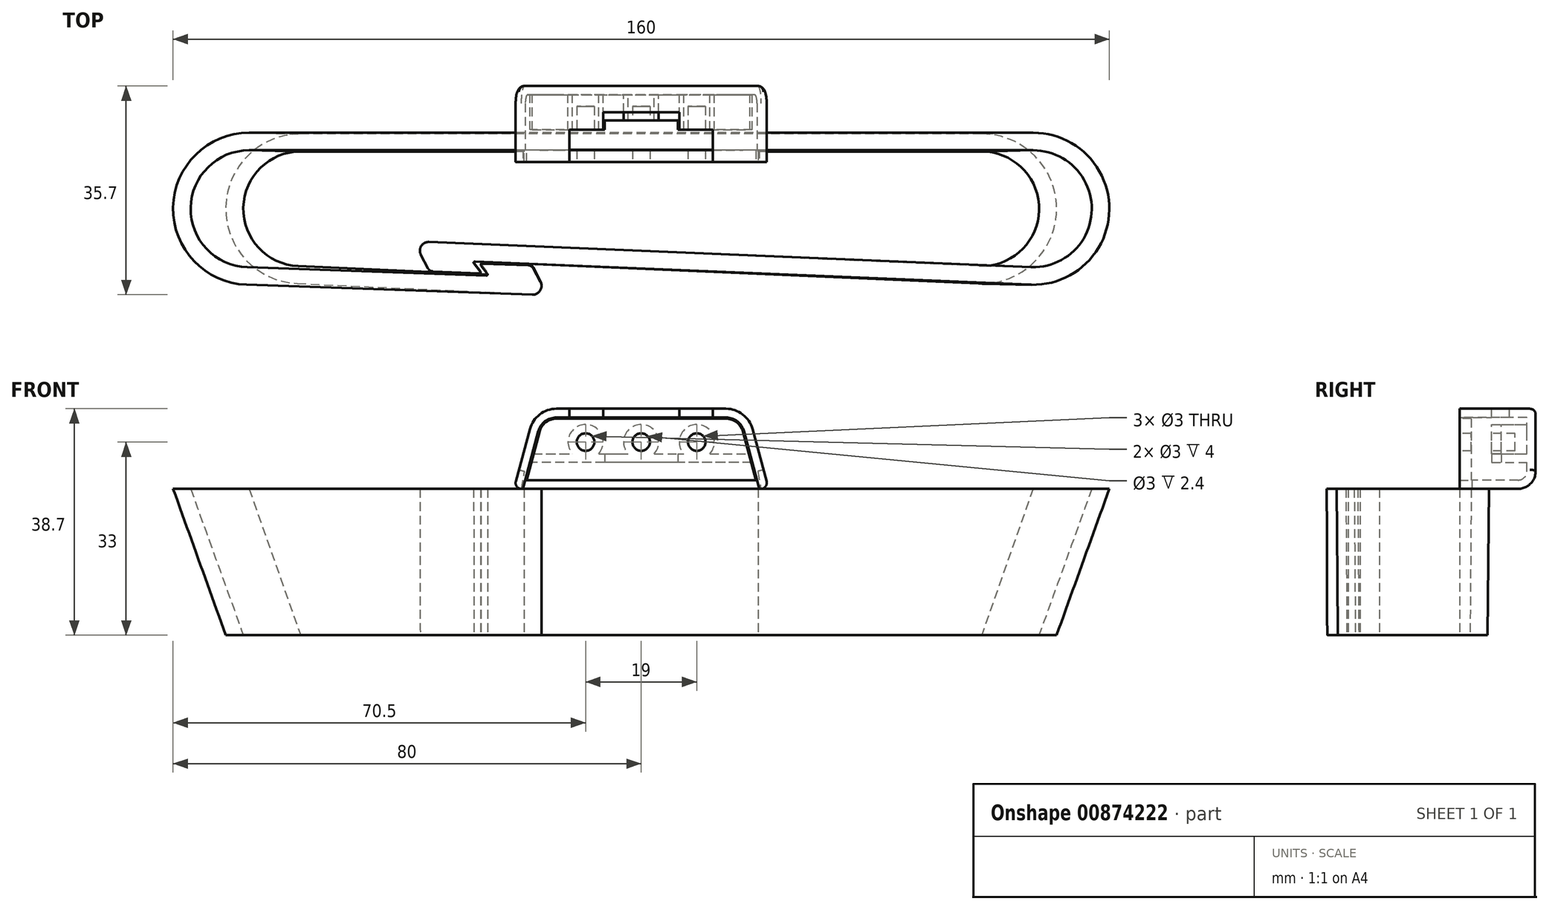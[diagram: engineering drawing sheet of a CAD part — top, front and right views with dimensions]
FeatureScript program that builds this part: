
annotation { "Feature Type Name" : "Feature", "Feature Type Description" : "" }
export const myFeature = defineFeature(function(context is Context, id is Id, definition is map)
    precondition{}
    {
        {
            var Q0;
            Q0=qCreatedBy(makeId("Top.planeOp"),FACE);
            var sketch = newSketch(context, id + "F0", { "sketchPlane" : qUnion([Q0])});
            skPoint(sketch, "E0.middle", {"position": v(0, 0) * mm});
            skArc(sketch, "E1", {"start": v(66.46, -12.99) * mm, "mid": v(80, -0.27) * mm, "end": v(67, 13) * mm});
            skLineSegment(sketch, "E2", {"start": v(67, 13) * mm, "end": v(-67, 13) * mm});
            skArc(sketch, "E3", {"start": v(-67, 13) * mm, "mid": v(-80, 0.23) * mm, "end": v(-67.45, -13) * mm});
            skLineSegment(sketch, "E4", {"start": v(66.46, -12.99) * mm, "end": v(-28.42, -9.01) * mm});
            skLineSegment(sketch, "E5", {"start": v(0, 13) * mm, "end": v(0, -10.2) * mm, "construction": true});
            skLineSegment(sketch, "E6", {"start": v(-16, 0) * mm, "end": v(-16, -14.79) * mm, "construction": true});
            skLineSegment(sketch, "E7", {"start": v(-67.45, -13) * mm, "end": v(-18.6, -14.7) * mm});
            skLineSegment(sketch, "E8", {"start": v(-67, 0) * mm, "end": v(-16, 0) * mm, "construction": true});
            skLineSegment(sketch, "E9.0", {"start": v(66.58, -10) * mm, "end": v(-36.26, -5.68) * mm});
            skLineSegment(sketch, "E9.1", {"start": v(-67.35, -10) * mm, "end": v(-26.46, -11.42) * mm});
            skArc(sketch, "E9.2", {"start": v(-67, 10) * mm, "mid": v(-77, 0.17) * mm, "end": v(-67.35, -10) * mm});
            skLineSegment(sketch, "E9.3", {"start": v(67, 10) * mm, "end": v(-67, 10) * mm});
            skArc(sketch, "E9.4", {"start": v(66.58, -10) * mm, "mid": v(77, -0.2) * mm, "end": v(67, 10) * mm});
            skLineSegment(sketch, "E10", {"start": v(-27.2, -9.4) * mm, "end": v(-19.29, -9.67) * mm});
            skLineSegment(sketch, "E11", {"start": v(-18.44, -10.2) * mm, "end": v(-17.22, -12.5) * mm});
            skPoint(sketch, "E12.visualSharp", {"position": v(-16, -14.79) * mm});
            skArc(sketch, "E12.filletArc", {"start": v(-18.6, -14.7) * mm, "mid": v(-17.27, -14) * mm, "end": v(-17.22, -12.5) * mm});
            skPoint(sketch, "E13.visualSharp", {"position": v(-18.71, -9.7) * mm});
            skArc(sketch, "E13.filletArc", {"start": v(-18.44, -10.2) * mm, "mid": v(-18.8, -9.82) * mm, "end": v(-19.29, -9.67) * mm});
            skPoint(sketch, "E14.visualSharp", {"position": v(-27.2, -9.4) * mm});
            skArc(sketch, "E14.filletArc", {"start": v(-27.2, -9.4) * mm, "mid": v(-27.4, -9.5) * mm, "end": v(-27.37, -9.72) * mm});
            skLineSegment(sketch, "E15", {"start": v(0, 0) * mm, "end": v(67, 0) * mm, "construction": true});
            skLineSegment(sketch, "E16", {"start": v(-28.59, -9.33) * mm, "end": v(-27.52, -10.72) * mm});
            skLineSegment(sketch, "E17", {"start": v(-27.69, -11.04) * mm, "end": v(-35.6, -10.71) * mm});
            skLineSegment(sketch, "E18", {"start": v(-36.45, -10.18) * mm, "end": v(-37.65, -7.87) * mm});
            skPoint(sketch, "E19.visualSharp", {"position": v(-36.18, -10.69) * mm});
            skArc(sketch, "E19.filletArc", {"start": v(-36.45, -10.18) * mm, "mid": v(-36.1, -10.56) * mm, "end": v(-35.6, -10.71) * mm});
            skPoint(sketch, "E20.visualSharp", {"position": v(-38.85, -5.57) * mm});
            skArc(sketch, "E20.filletArc", {"start": v(-36.26, -5.68) * mm, "mid": v(-37.59, -6.38) * mm, "end": v(-37.65, -7.87) * mm});
            skArc(sketch, "E21.filletArc", {"start": v(-27.69, -11.04) * mm, "mid": v(-27.5, -10.94) * mm, "end": v(-27.52, -10.72) * mm});
            skPoint(sketch, "E22.visualSharp", {"position": v(-28.85, -9) * mm});
            skArc(sketch, "E22.filletArc", {"start": v(-28.42, -9.01) * mm, "mid": v(-28.6, -9.12) * mm, "end": v(-28.59, -9.33) * mm});
            skLineSegment(sketch, "E23", {"start": v(-16, 0) * mm, "end": v(0, 0) * mm, "construction": true});
            skArc(sketch, "E24", {"start": v(-26.46, -11.42) * mm, "mid": v(-26.27, -11.31) * mm, "end": v(-26.3, -11.1) * mm});
            skLineSegment(sketch, "E25", {"start": v(-27.37, -9.72) * mm, "end": v(-26.3, -11.1) * mm});
            skLineSegment(sketch, "E26", {"start": v(-27.37, -9.47) * mm, "end": v(-27.37, -10.97) * mm, "construction": true});
            skLineSegment(sketch, "E27", {"start": v(-27.52, -10.72) * mm, "end": v(-27.52, -9.22) * mm, "construction": true});
            skSolve(sketch);
        }
        {
            var Q0;
            Q0=qCreatedBy(makeId("Top.planeOp"),FACE);
            cPlane(context, id + "F1", {"entities" : qUnion([Q0]), "cplaneType" : CPlaneType.OFFSET, "offset" : 25 * mm, "oppositeDirection" : true, "width" : 150 * mm, "height" : 150 * mm});
        }
        {
            var Q0;
            Q0=qCreatedBy(id+"F1.planeOp",FACE);
            var sketch = newSketch(context, id + "F2", { "sketchPlane" : qUnion([Q0])});
            skPoint(sketch, "E28.middle", {"position": v(0, 0) * mm});
            skArc(sketch, "E29", {"start": v(57.64, -12.79) * mm, "mid": v(71, -0.28) * mm, "end": v(58.2, 12.8) * mm});
            skLineSegment(sketch, "E30", {"start": v(58.2, 12.8) * mm, "end": v(-58.2, 12.8) * mm});
            skArc(sketch, "E31", {"start": v(-58.2, 12.8) * mm, "mid": v(-71, 0.3) * mm, "end": v(-58.78, -12.79) * mm});
            skLineSegment(sketch, "E32", {"start": v(57.64, -12.79) * mm, "end": v(-28.37, -9.03) * mm});
            skLineSegment(sketch, "E33", {"start": v(0, 12.8) * mm, "end": v(0, -10.27) * mm, "construction": true});
            skLineSegment(sketch, "E34", {"start": v(-16, 0) * mm, "end": v(-16, -14.73) * mm, "construction": true});
            skLineSegment(sketch, "E35", {"start": v(-58.78, -12.79) * mm, "end": v(-18.6, -14.61) * mm});
            skLineSegment(sketch, "E36", {"start": v(-58.2, 0) * mm, "end": v(-16, 0) * mm, "construction": true});
            skLineSegment(sketch, "E37.0", {"start": v(57.77, -9.8) * mm, "end": v(-36.2, -5.69) * mm});
            skLineSegment(sketch, "E37.1", {"start": v(-58.64, -9.79) * mm, "end": v(-26.42, -11.25) * mm});
            skArc(sketch, "E37.2", {"start": v(-58.2, 9.8) * mm, "mid": v(-68, 0.22) * mm, "end": v(-58.64, -9.79) * mm});
            skLineSegment(sketch, "E37.3", {"start": v(58.2, 9.8) * mm, "end": v(-58.2, 9.8) * mm});
            skArc(sketch, "E37.4", {"start": v(57.77, -9.8) * mm, "mid": v(68, -0.21) * mm, "end": v(58.2, 9.8) * mm});
            skLineSegment(sketch, "E38", {"start": v(-27.15, -9.22) * mm, "end": v(-19.23, -9.58) * mm});
            skLineSegment(sketch, "E39", {"start": v(-18.4, -10.12) * mm, "end": v(-17.2, -12.42) * mm});
            skPoint(sketch, "E40.visualSharp", {"position": v(-16, -14.73) * mm});
            skArc(sketch, "E40.filletArc", {"start": v(-18.6, -14.61) * mm, "mid": v(-17.26, -13.92) * mm, "end": v(-17.2, -12.42) * mm});
            skPoint(sketch, "E41.visualSharp", {"position": v(-18.66, -9.6) * mm});
            skArc(sketch, "E41.filletArc", {"start": v(-18.4, -10.12) * mm, "mid": v(-18.74, -9.73) * mm, "end": v(-19.23, -9.58) * mm});
            skPoint(sketch, "E42.visualSharp", {"position": v(-27.15, -9.22) * mm});
            skArc(sketch, "E42.filletArc", {"start": v(-27.15, -9.22) * mm, "mid": v(-27.33, -9.33) * mm, "end": v(-27.32, -9.54) * mm});
            skLineSegment(sketch, "E43", {"start": v(0, 0) * mm, "end": v(58.2, 0) * mm, "construction": true});
            skLineSegment(sketch, "E44", {"start": v(-28.53, -9.35) * mm, "end": v(-27.47, -10.74) * mm});
            skLineSegment(sketch, "E45", {"start": v(-27.63, -11.07) * mm, "end": v(-35.55, -10.72) * mm});
            skLineSegment(sketch, "E46", {"start": v(-36.4, -10.18) * mm, "end": v(-37.6, -7.88) * mm});
            skPoint(sketch, "E47.visualSharp", {"position": v(-36.13, -10.7) * mm});
            skArc(sketch, "E47.filletArc", {"start": v(-36.4, -10.18) * mm, "mid": v(-36.04, -10.57) * mm, "end": v(-35.55, -10.72) * mm});
            skPoint(sketch, "E48.visualSharp", {"position": v(-38.8, -5.57) * mm});
            skArc(sketch, "E48.filletArc", {"start": v(-36.2, -5.69) * mm, "mid": v(-37.53, -6.38) * mm, "end": v(-37.6, -7.88) * mm});
            skArc(sketch, "E49.filletArc", {"start": v(-27.63, -11.07) * mm, "mid": v(-27.45, -10.96) * mm, "end": v(-27.47, -10.74) * mm});
            skPoint(sketch, "E50.visualSharp", {"position": v(-28.8, -9.01) * mm});
            skArc(sketch, "E50.filletArc", {"start": v(-28.37, -9.03) * mm, "mid": v(-28.55, -9.14) * mm, "end": v(-28.53, -9.35) * mm});
            skLineSegment(sketch, "E51", {"start": v(-16, 0) * mm, "end": v(0, 0) * mm, "construction": true});
            skArc(sketch, "E52", {"start": v(-26.42, -11.25) * mm, "mid": v(-26.23, -11.15) * mm, "end": v(-26.25, -10.93) * mm});
            skLineSegment(sketch, "E53", {"start": v(-27.32, -9.54) * mm, "end": v(-26.25, -10.93) * mm});
            skLineSegment(sketch, "E54", {"start": v(-27.32, -9.3) * mm, "end": v(-27.32, -10.8) * mm, "construction": true});
            skLineSegment(sketch, "E55", {"start": v(-27.47, -10.74) * mm, "end": v(-27.47, -9.24) * mm, "construction": true});
            skSolve(sketch);
        }
        {
            var Q0;
            Q0=qSketchRegion(id+"F0",true);
            var Q1;
            Q1=qSketchRegion(id+"F2",true);
            loft(context, id + "F3", {"sheetProfilesArray" : [{ "sheetProfileEntities" : qUnion([Q0]) }, { "sheetProfileEntities" : qUnion([Q1]) }]});
        }
        {
            var Q0;
            Q0=qCreatedBy(makeId("Top.planeOp"),FACE);
            var sketch = newSketch(context, id + "F4", { "sketchPlane" : qUnion([Q0])});
            skLineSegment(sketch, "E56", {"start": v(20, 10) * mm, "end": v(20, 8) * mm});
            skLineSegment(sketch, "E57", {"start": v(-20, 8) * mm, "end": v(-20, 10) * mm});
            skLineSegment(sketch, "E58", {"start": v(-20, 10) * mm, "end": v(20, 10) * mm});
            skLineSegment(sketch, "E59", {"start": v(0, 8) * mm, "end": v(0, 10) * mm, "construction": true});
            skPoint(sketch, "E59.endSnap0", {"position": v(0, 10) * mm});
            skLineSegment(sketch, "E60", {"start": v(-20, 8) * mm, "end": v(20, 8) * mm});
            skSolve(sketch);
        }
        {
            var Q0;
            Q0=qSketchRegion(id+"F4",true);
            extrude(context, id + "F5", {"entities" : qUnion([Q0]), "operationType" : NewBodyOperationType.ADD, "depth" : 12 * mm, "offsetDistance" : 25 * mm, "hasSecondDirection" : true, "secondDirectionOppositeDirection" : true, "secondDirectionDepth" : 25 * mm});
        }
        {
            var Q0;
            Q0=makeQuery(id+"F5.opExtrude","SWEPT_FACE",FACE,{"disambiguationData":[OSD([sQuery(id+"F4.wireOp",EDGE,"E60")])]});
            var sketch = newSketch(context, id + "F6", { "sketchPlane" : qUnion([Q0])});
            skLineSegment(sketch, "E61", {"start": v(0, 12) * mm, "end": v(0, 8) * mm, "construction": true});
            skCircle(sketch, "E62", {"center": v(0, 8) * mm, "radius": 1.5 * mm});
            skCircle(sketch, "E63", {"center": v(9.5, 8) * mm, "radius": 1.5 * mm});
            skCircle(sketch, "E64", {"center": v(-9.5, 8) * mm, "radius": 1.5 * mm});
            skSolve(sketch);
        }
        {
            var Q0;
            Q0=qSketchRegion(id+"F6",true);
            extrude(context, id + "F7", {"entities" : qUnion([Q0]), "operationType" : NewBodyOperationType.REMOVE, "endBound" : BoundingType.THROUGH_ALL, "oppositeDirection" : true, "depth" : 25 * mm, "offsetDistance" : 25 * mm});
        }
        {
            var Q0;
            Q0=makeQuery(id+"F5.opExtrude","CAP_EDGE",EDGE,{"disambiguationData":[OSD([sQuery(id+"F4.wireOp",EDGE,"E57")])],"isStart":false});
            var Q1;
            Q1=makeQuery(id+"F5.opExtrude","CAP_EDGE",EDGE,{"disambiguationData":[OSD([sQuery(id+"F4.wireOp",EDGE,"E56")])],"isStart":false});
            chamfer(context, id + "F8", {"entities" : qUnion([Q0, Q1]), "chamferType" : ChamferType.OFFSET_ANGLE, "width" : 12 * mm, "oppositeDirection" : false, "angle" : 15 * degree, "tangentPropagation" : true});
        }
        {
            var Q0;
            {var subQ0=sQuery(id+"F4.wireOp",EDGE,"E57");Q0=makeQuery(id+"F8.opChamfer","BLEND_EDGE",EDGE,{"blendedFrom":[makeQuery(id+"F5.opExtrude","CAP_EDGE",EDGE,{"disambiguationData":[OSD([subQ0])],"isStart":false}),makeQuery(id+"F5.opExtrude","CAP_FACE",FACE,{"disambiguationData":[OSD([sQuery(id+"F4.wireOp",EDGE,"E56"),sQuery(id+"F4.wireOp",EDGE,"wCvbTNE0-mzVd-2HxN-2LCz-JJ2DgGp3YGLQ"),subQ0,sQuery(id+"F4.wireOp",EDGE,"E58")])],"isStart":false})],"blendedInto":[makeQuery(id+"F5.opExtrude","CAP_FACE",FACE,{"disambiguationData":[OSD([sQuery(id+"F4.wireOp",EDGE,"E56"),sQuery(id+"F4.wireOp",EDGE,"wCvbTNE0-mzVd-2HxN-2LCz-JJ2DgGp3YGLQ"),subQ0,sQuery(id+"F4.wireOp",EDGE,"E58")])],"isStart":false})]});}
            var Q1;
            {var subQ0=sQuery(id+"F4.wireOp",EDGE,"E56");Q1=makeQuery(id+"F8.opChamfer","BLEND_EDGE",EDGE,{"blendedFrom":[makeQuery(id+"F5.opExtrude","CAP_EDGE",EDGE,{"disambiguationData":[OSD([subQ0])],"isStart":false}),makeQuery(id+"F5.opExtrude","CAP_FACE",FACE,{"disambiguationData":[OSD([subQ0,sQuery(id+"F4.wireOp",EDGE,"wCvbTNE0-mzVd-2HxN-2LCz-JJ2DgGp3YGLQ"),sQuery(id+"F4.wireOp",EDGE,"E57"),sQuery(id+"F4.wireOp",EDGE,"E58")])],"isStart":false})],"blendedInto":[makeQuery(id+"F5.opExtrude","CAP_FACE",FACE,{"disambiguationData":[OSD([subQ0,sQuery(id+"F4.wireOp",EDGE,"wCvbTNE0-mzVd-2HxN-2LCz-JJ2DgGp3YGLQ"),sQuery(id+"F4.wireOp",EDGE,"E57"),sQuery(id+"F4.wireOp",EDGE,"E58")])],"isStart":false})]});}
            fillet(context, id + "F9", {"entities" : qUnion([Q0, Q1]), "radius" : 3 * mm, "tangentPropagation" : true, "allowEdgeOverflow" : false});
        }
        {
            var Q0;
            Q0=makeQuery(id+"F5.opExtrude","SWEPT_FACE",FACE,{"disambiguationData":[OSD([sQuery(id+"F4.wireOp",EDGE,"E60")])]});
            cPlane(context, id + "F10", {"entities" : qUnion([Q0]), "cplaneType" : CPlaneType.OFFSET, "offset" : 0 * mm, "oppositeDirection" : true, "width" : 150 * mm, "height" : 150 * mm});
        }
        {
            var Q0;
            Q0=qCreatedBy(id+"F10.planeOp",FACE);
            var sketch = newSketch(context, id + "F11", { "sketchPlane" : qUnion([Q0])});
            skLineSegment(sketch, "E65.0", {"start": v(-19.02, 10.22) * mm, "end": v(-21.76, 0) * mm});
            skLineSegment(sketch, "E65.1", {"start": v(21.76, 0) * mm, "end": v(19.02, 10.22) * mm});
            skArc(sketch, "E65.2", {"start": v(19.02, 10.22) * mm, "mid": v(17.34, 12.73) * mm, "end": v(14.48, 13.7) * mm});
            skLineSegment(sketch, "E65.3", {"start": v(-14.48, 13.7) * mm, "end": v(14.48, 13.7) * mm});
            skArc(sketch, "E65.4", {"start": v(-14.48, 13.7) * mm, "mid": v(-17.34, 12.73) * mm, "end": v(-19.02, 10.22) * mm});
            skLineSegment(sketch, "E66", {"start": v(-21.76, 0) * mm, "end": v(21.76, 0) * mm});
            skSolve(sketch);
        }
        {
            var Q0;
            Q0=qSketchRegion(id+"F11",true);
            extrude(context, id + "F12", {"entities" : qUnion([Q0]), "oppositeDirection" : true, "depth" : 13 * mm, "offsetDistance" : 25 * mm});
        }
        {
            var Q0;
            Q0=makeQuery(id+"F12.opExtrude","CAP_EDGE",EDGE,{"disambiguationData":[OSD([sQuery(id+"F11.wireOp",EDGE,"E66")])],"isStart":false});
            fillet(context, id + "F13", {"entities" : qUnion([Q0]), "radius" : 3 * mm, "tangentPropagation" : true, "allowEdgeOverflow" : false});
        }
        {
            var Q0;
            Q0=makeQuery(id+"F12.opExtrude","CAP_FACE",FACE,{"disambiguationData":[OSD([sQuery(id+"F11.wireOp",EDGE,"E65.0"),sQuery(id+"F11.wireOp",EDGE,"E65.1"),sQuery(id+"F11.wireOp",EDGE,"E65.2"),sQuery(id+"F11.wireOp",EDGE,"E65.3"),sQuery(id+"F11.wireOp",EDGE,"E65.4"),sQuery(id+"F11.wireOp",EDGE,"E66")])],"isStart":true});
            shell(context, id + "F14", {"entities" : qUnion([Q0]), "thickness" : 1.5 * mm});
        }
        {
            var Q0;
            Q0=makeQuery(id+"F12.opExtrude","CAP_FACE",FACE,{"disambiguationData":[OSD([sQuery(id+"F11.wireOp",EDGE,"E65.0"),sQuery(id+"F11.wireOp",EDGE,"E65.1"),sQuery(id+"F11.wireOp",EDGE,"E65.2"),sQuery(id+"F11.wireOp",EDGE,"E65.3"),sQuery(id+"F11.wireOp",EDGE,"E65.4"),sQuery(id+"F11.wireOp",EDGE,"E66")])],"isStart":true});
            var sketch = newSketch(context, id + "F15", { "sketchPlane" : qUnion([Q0])});
            skLineSegment(sketch, "E67", {"start": v(-19.8, 1.5) * mm, "end": v(19.8, 1.5) * mm});
            skLineSegment(sketch, "E68", {"start": v(19.8, 1.5) * mm, "end": v(20.2, 0) * mm});
            skLineSegment(sketch, "E69", {"start": v(20.2, 0) * mm, "end": v(-20.2, 0) * mm});
            skLineSegment(sketch, "E70", {"start": v(-20.2, 0) * mm, "end": v(-19.8, 1.5) * mm});
            skPoint(sketch, "E71", {"position": v(0, 0) * mm});
            skSolve(sketch);
        }
        {
            var Q0;
            Q0=qSketchRegion(id+"F15",true);
            extrude(context, id + "F16", {"entities" : qUnion([Q0]), "operationType" : NewBodyOperationType.REMOVE, "oppositeDirection" : true, "depth" : 2.1 * mm, "offsetDistance" : 25 * mm});
        }
        {
            var Q0;
            Q0=makeQuery(id+"F12.opExtrude","SWEPT_EDGE",EDGE,{"disambiguationData":[OSD([sQuery(id+"F11.wireOp",EDGE,"E65.1"),sQuery(id+"F11.wireOp",EDGE,"E66")])]});
            fillet(context, id + "F17", {"entities" : qUnion([Q0]), "radius" : 1 * mm, "tangentPropagation" : true, "allowEdgeOverflow" : false});
        }
        {
            var Q0;
            Q0=makeQuery(id+"F14.opShell","OFFSET_FACE",FACE,{"disambiguationData":[OSD([sQuery(id+"F11.wireOp",EDGE,"E65.0"),sQuery(id+"F11.wireOp",EDGE,"E65.1"),sQuery(id+"F11.wireOp",EDGE,"E65.2"),sQuery(id+"F11.wireOp",EDGE,"E65.3"),sQuery(id+"F11.wireOp",EDGE,"E65.4"),sQuery(id+"F11.wireOp",EDGE,"E66")])]});
            var sketch = newSketch(context, id + "F18", { "sketchPlane" : qUnion([Q0])});
            skCircle(sketch, "E72", {"center": v(0, 8) * mm, "radius": 3 * mm});
            skCircle(sketch, "E73", {"center": v(9.5, 8) * mm, "radius": 3 * mm});
            skCircle(sketch, "E74", {"center": v(-9.5, 8) * mm, "radius": 3 * mm});
            skLineSegment(sketch, "E75", {"start": v(-18.6, 6) * mm, "end": v(18.6, 6) * mm});
            skLineSegment(sketch, "E76", {"start": v(18.6, 6) * mm, "end": v(19, 4.5) * mm});
            skLineSegment(sketch, "E77", {"start": v(19, 4.5) * mm, "end": v(-19, 4.5) * mm});
            skLineSegment(sketch, "E78", {"start": v(-19, 4.5) * mm, "end": v(-18.6, 6) * mm});
            skSolve(sketch);
        }
        {
            var Q0;
            Q0=makeQuery(id+"F18.imprint","IMPRINT",FACE,{"disambiguationData":[TD([[makeQuery(id+"F18.imprint","IMPRINT",EDGE,{"derivedFrom":sQuery(id+"F18.wireOp",EDGE,"E74")}),1.0]])]});
            var Q1;
            Q1=makeQuery(id+"F18.imprint","IMPRINT",FACE,{"disambiguationData":[TD([[makeQuery(id+"F18.imprint","IMPRINT",EDGE,{"derivedFrom":sQuery(id+"F18.wireOp",EDGE,"E73")}),1.0]])]});
            var Q2;
            {var subQ0=sQuery(id+"F18.wireOp",EDGE,"E76");Q2=makeQuery(id+"F18.imprint","IMPRINT",FACE,{"disambiguationData":[TD([[makeQuery(id+"F18.imprint","IMPRINT",EDGE,{"derivedFrom":subQ0}),1.0]])]});}
            var Q3;
            {var subQ0=sQuery(id+"F18.wireOp",EDGE,"E75");var subQ1=sQuery(id+"F18.wireOp",EDGE,"E72");var subQ2=makeQuery(id+"F18.imprint","INTERSECT",VERTEX,{"disambiguationData":[OD(0.0)],"derivedFrom":[subQ1,subQ0]});Q3=makeQuery(id+"F18.imprint","IMPRINT",FACE,{"disambiguationData":[TD([[makeQuery(id+"F18.imprint","IMPRINT",EDGE,{"disambiguationData":[TD([[subQ2,1.0]])],"derivedFrom":subQ1}),1.0]])]});}
            var Q4;
            {var subQ0=sQuery(id+"F18.wireOp",EDGE,"E75");var subQ1=sQuery(id+"F18.wireOp",EDGE,"E72");var subQ2=makeQuery(id+"F18.imprint","INTERSECT",VERTEX,{"disambiguationData":[OD(0.0)],"derivedFrom":[subQ1,subQ0]});Q4=makeQuery(id+"F18.imprint","IMPRINT",FACE,{"disambiguationData":[TD([[makeQuery(id+"F18.imprint","IMPRINT",EDGE,{"disambiguationData":[TD([[subQ2,-1.0]])],"derivedFrom":subQ1}),1.0]])]});}
            extrude(context, id + "F19", {"entities" : qUnion([Q0, Q1, Q2, Q3, Q4]), "operationType" : NewBodyOperationType.ADD, "depth" : 6 * mm, "offsetDistance" : 25 * mm});
        }
        {
            var Q0;
            Q0=makeQuery(id+"F6.imprint","IMPRINT",FACE,{"disambiguationData":[TD([[makeQuery(id+"F6.imprint","IMPRINT",EDGE,{"derivedFrom":sQuery(id+"F6.wireOp",EDGE,"E64")}),1.0]])]});
            var Q1;
            Q1=makeQuery(id+"F6.imprint","IMPRINT",FACE,{"disambiguationData":[TD([[makeQuery(id+"F6.imprint","IMPRINT",EDGE,{"derivedFrom":sQuery(id+"F6.wireOp",EDGE,"E62")}),1.0]])]});
            var Q2;
            Q2=makeQuery(id+"F6.imprint","IMPRINT",FACE,{"disambiguationData":[TD([[makeQuery(id+"F6.imprint","IMPRINT",EDGE,{"derivedFrom":sQuery(id+"F6.wireOp",EDGE,"E63")}),1.0]])]});
            extrude(context, id + "F20", {"entities" : qUnion([Q0, Q1, Q2]), "operationType" : NewBodyOperationType.REMOVE, "oppositeDirection" : true, "depth" : (11 - 1.5) * mm, "offsetDistance" : 25 * mm});
        }
        {
            var Q0;
            Q0=makeQuery(id+"F12.opExtrude","SWEPT_FACE",FACE,{"disambiguationData":[OSD([sQuery(id+"F11.wireOp",EDGE,"E65.3")])]});
            var sketch = newSketch(context, id + "F21", { "sketchPlane" : qUnion([Q0])});
            skLineSegment(sketch, "E79", {"start": v(-12.25, 8) * mm, "end": v(-12.25, 13.5) * mm});
            skLineSegment(sketch, "E80", {"start": v(-12.25, 13.5) * mm, "end": v(-6.5, 13.5) * mm});
            skLineSegment(sketch, "E81", {"start": v(-6.5, 13.5) * mm, "end": v(-6.5, 16.5) * mm});
            skLineSegment(sketch, "E82", {"start": v(-6.5, 16.5) * mm, "end": v(6.5, 16.5) * mm});
            skLineSegment(sketch, "E83", {"start": v(6.5, 16.5) * mm, "end": v(6.5, 13.5) * mm});
            skLineSegment(sketch, "E84", {"start": v(6.5, 13.5) * mm, "end": v(12.25, 13.5) * mm});
            skLineSegment(sketch, "E85", {"start": v(12.25, 13.5) * mm, "end": v(12.25, 8) * mm});
            skLineSegment(sketch, "E86", {"start": v(12.25, 8) * mm, "end": v(-12.25, 8) * mm});
            skPoint(sketch, "E87", {"position": v(0, 8) * mm});
            skSolve(sketch);
        }
        {
            var Q0;
            Q0=qSketchRegion(id+"F21",true);
            extrude(context, id + "F22", {"entities" : qUnion([Q0]), "operationType" : NewBodyOperationType.REMOVE, "oppositeDirection" : true, "depth" : 1.5 * mm, "offsetDistance" : 25 * mm});
        }
        {
            var Q0;
            {var subQ0=sQuery(id+"F11.wireOp",EDGE,"E66");Q0=makeQuery(id+"F14.opShell","OFFSET_FACE",FACE,{"disambiguationData":[OSD([subQ0]),TDD([makeQuery(id+"F12.opExtrude","SWEPT_FACE",FACE,{"disambiguationData":[OSD([subQ0])]})])]});}
            var sketch = newSketch(context, id + "F23", { "sketchPlane" : qUnion([Q0])});
            skLineSegment(sketch, "E88.bottom", {"start": v(6.25, 10.1) * mm, "end": v(-6.25, 10.1) * mm});
            skLineSegment(sketch, "E88.top", {"start": v(6.25, 15.1) * mm, "end": v(-6.25, 15.1) * mm});
            skLineSegment(sketch, "E88.left", {"start": v(6.25, 10.1) * mm, "end": v(6.25, 15.1) * mm});
            skLineSegment(sketch, "E88.right", {"start": v(-6.25, 10.1) * mm, "end": v(-6.25, 15.1) * mm});
            skPoint(sketch, "E89", {"position": v(0, 10.1) * mm});
            skSolve(sketch);
        }
        {
            var Q0;
            Q0=makeQuery(id+"F23.imprint","IMPRINT",FACE,{"disambiguationData":[TD([[makeQuery(id+"F23.imprint","IMPRINT",EDGE,{"derivedFrom":sQuery(id+"F23.wireOp",EDGE,"E88.bottom")}),1.0]])]});
            extrude(context, id + "F24", {"entities" : qUnion([Q0]), "operationType" : NewBodyOperationType.REMOVE, "depth" : 25 * mm, "offsetDistance" : 25 * mm});
        }
    });
